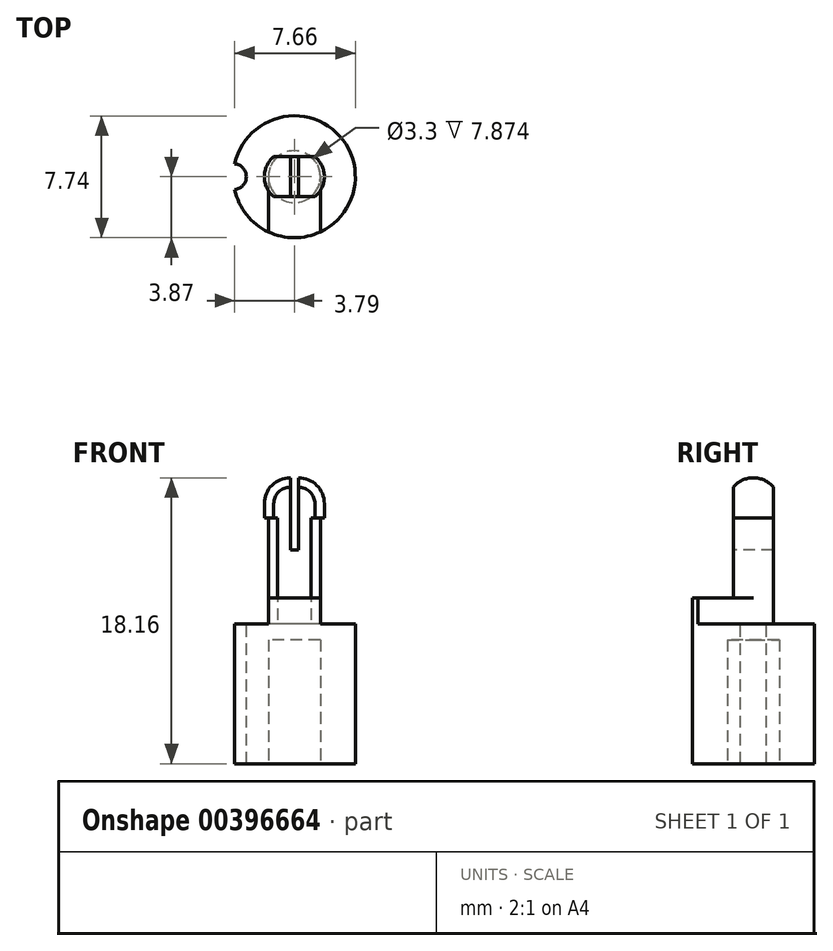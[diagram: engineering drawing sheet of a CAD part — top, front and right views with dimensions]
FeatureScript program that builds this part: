
annotation { "Feature Type Name" : "Feature", "Feature Type Description" : "" }
export const myFeature = defineFeature(function(context is Context, id is Id, definition is map)
    precondition{}
    {
        {
            var Q0;
            Q0=qCreatedBy(makeId("Top.planeOp"),FACE);
            var sketch = newSketch(context, id + "F0", { "sketchPlane" : qUnion([Q0])});
            skCircle(sketch, "E0", {"center": v(0, 0) * mm, "radius": 1.65 * mm});
            skCircle(sketch, "E1", {"center": v(0, 0) * mm, "radius": 3.87 * mm});
            skSolve(sketch);
        }
        {
            var Q0;
            Q0=makeQuery(id+"F0.imprint","IMPRINT",FACE,{"disambiguationData":[TD([[makeQuery(id+"F0.imprint","IMPRINT",EDGE,{"derivedFrom":sQuery(id+"F0.wireOp",EDGE,"E0")}),-1.0]])]});
            var Q1;
            Q1=sQuery(id+"F0.wireOp",EDGE,"E1");
            var Q2;
            Q2=sQuery(id+"F0.wireOp",EDGE,"E0");
            extrude(context, id + "F1", {"entities" : qUnion([Q0]), "surfaceEntities" : qUnion([Q1, Q2]), "depth" : 7.87 * mm});
        }
        {
            var Q0;
            Q0=makeQuery(id+"F1.opExtrude","CAP_FACE",FACE,{"disambiguationData":[OSD([sQuery(id+"F0.wireOp",EDGE,"E0"),sQuery(id+"F0.wireOp",EDGE,"E1")])],"isStart":false});
            var sketch = newSketch(context, id + "F2", { "sketchPlane" : qUnion([Q0])});
            skCircle(sketch, "E2", {"center": v(0, 0) * mm, "radius": 3.87 * mm});
            skSolve(sketch);
        }
        {
            var Q0;
            Q0 = qSketchRegion(id + "F2", true);
            extrude(context, id + "F3", {"entities" : qUnion([Q0]), "operationType" : NewBodyOperationType.ADD, "depth" : 1.02 * mm});
        }
        {
            var Q0;
            Q0=makeQuery(id+"F3.opExtrude","CAP_FACE",FACE,{"disambiguationData":[OSD([sQuery(id+"F2.wireOp",EDGE,"E2")])],"isStart":false});
            var sketch = newSketch(context, id + "F4", { "sketchPlane" : qUnion([Q0])});
            skCircle(sketch, "E3", {"center": v(-3.87, 0) * mm, "radius": 0.83 * mm});
            skLineSegment(sketch, "E4", {"start": v(-1.05, 1.27) * mm, "end": v(0, 1.27) * mm});
            skArc(sketch, "E5", {"start": v(-1.05, 1.27) * mm, "mid": v(-1.5, 0.7) * mm, "end": v(-1.65, 0) * mm});
            skLineSegment(sketch, "E6.MirrorCS", {"start": v(1.05, 1.27) * mm, "end": v(0, 1.27) * mm});
            skArc(sketch, "E7.MirrorCS", {"start": v(1.05, 1.27) * mm, "mid": v(1.5, 0.7) * mm, "end": v(1.65, 0) * mm});
            skLineSegment(sketch, "E8", {"start": v(-1.65, 0) * mm, "end": v(-1.65, -3.5) * mm});
            skLineSegment(sketch, "E9", {"start": v(1.65, 0) * mm, "end": v(1.65, -3.5) * mm});
            skSolve(sketch);
        }
        {
            var Q0;
            {var subQ0=sQuery(id+"F4.wireOp",EDGE,"E3");var subQ1=makeQuery(id+"F3.opExtrude","CAP_EDGE",EDGE,{"disambiguationData":[OSD([sQuery(id+"F2.wireOp",EDGE,"E2")])],"isStart":false});var subQ2=makeQuery(id+"F4.imprint","INTERSECT",VERTEX,{"disambiguationData":[OD(0.0)],"derivedFrom":[subQ1,subQ0]});Q0=makeQuery(id+"F4.imprint","IMPRINT",FACE,{"disambiguationData":[TD([[makeQuery(id+"F4.imprint","IMPRINT",EDGE,{"disambiguationData":[TD([[subQ2,-1.0]])],"derivedFrom":subQ0}),1.0]])]});}
            var Q1;
            Q1=makeQuery(id+"F1.opExtrude","CAP_FACE",FACE,{"disambiguationData":[OSD([sQuery(id+"F0.wireOp",EDGE,"E0"),sQuery(id+"F0.wireOp",EDGE,"E1")])],"isStart":true});
            extrude(context, id + "F5", {"entities" : qUnion([Q0]), "operationType" : NewBodyOperationType.REMOVE, "endBound" : BoundingType.UP_TO_SURFACE, "oppositeDirection" : true, "endBoundEntityFace" : qUnion([Q1]), "depth" : 25.4 * mm});
        }
        {
            var Q0;
            Q0=makeQuery(id+"F4.imprint","IMPRINT",FACE,{"disambiguationData":[TD([[makeQuery(id+"F4.imprint","IMPRINT",EDGE,{"derivedFrom":sQuery(id+"F4.wireOp",EDGE,"E4")}),-1.0]])]});
            extrude(context, id + "F6", {"entities" : qUnion([Q0]), "operationType" : NewBodyOperationType.ADD, "depth" : 1.65 * mm});
        }
        {
            var Q0;
            Q0=makeQuery(id+"F6.opExtrude","CAP_FACE",FACE,{"disambiguationData":[OSD([sQuery(id+"F2.wireOp",EDGE,"E2"),sQuery(id+"F4.wireOp",EDGE,"E4"),sQuery(id+"F4.wireOp",EDGE,"E5"),sQuery(id+"F4.wireOp",EDGE,"E6.MirrorCS"),sQuery(id+"F4.wireOp",EDGE,"E7.MirrorCS"),sQuery(id+"F4.wireOp",EDGE,"E8"),sQuery(id+"F4.wireOp",EDGE,"E9")])],"isStart":false});
            var sketch = newSketch(context, id + "F7", { "sketchPlane" : qUnion([Q0])});
            skCircle(sketch, "E10", {"center": v(-8.64, -1.16) * mm, "radius": 0.83 * mm});
            skLineSegment(sketch, "E11", {"start": v(-1.05, 1.27) * mm, "end": v(0, 1.27) * mm});
            skArc(sketch, "E12", {"start": v(-1.05, 1.27) * mm, "mid": v(-1.5, 0.7) * mm, "end": v(-1.65, 0) * mm});
            skLineSegment(sketch, "E13.MirrorCS", {"start": v(1.05, 1.27) * mm, "end": v(0, 1.27) * mm});
            skArc(sketch, "E14.MirrorCS", {"start": v(1.05, 1.27) * mm, "mid": v(1.5, 0.7) * mm, "end": v(1.65, 0) * mm});
            skLineSegment(sketch, "E15.MirrorCS", {"start": v(-1.05, -1.27) * mm, "end": v(0, -1.27) * mm});
            skArc(sketch, "E16.MirrorCS", {"start": v(-1.05, -1.27) * mm, "mid": v(-1.5, -0.7) * mm, "end": v(-1.65, 0) * mm});
            skLineSegment(sketch, "E17.MirrorCS", {"start": v(1.05, -1.27) * mm, "end": v(0, -1.27) * mm});
            skArc(sketch, "E18.MirrorCS", {"start": v(1.05, -1.27) * mm, "mid": v(1.5, -0.7) * mm, "end": v(1.65, 0) * mm});
            skSolve(sketch);
        }
        {
            var Q0;
            Q0=makeQuery(id+"F7.imprint","IMPRINT",FACE,{"disambiguationData":[TD([[makeQuery(id+"F7.imprint","IMPRINT",EDGE,{"derivedFrom":sQuery(id+"F7.wireOp",EDGE,"E11")}),1.0]])]});
            extrude(context, id + "F8", {"entities" : qUnion([Q0]), "operationType" : NewBodyOperationType.ADD, "depth" : 5.08 * mm});
        }
        {
            var Q0;
            Q0=makeQuery(id+"F8.opExtrude","CAP_FACE",FACE,{"disambiguationData":[OSD([sQuery(id+"F7.wireOp",EDGE,"E11"),sQuery(id+"F7.wireOp",EDGE,"E12"),sQuery(id+"F7.wireOp",EDGE,"E13.MirrorCS"),sQuery(id+"F7.wireOp",EDGE,"E14.MirrorCS"),sQuery(id+"F7.wireOp",EDGE,"E15.MirrorCS"),sQuery(id+"F7.wireOp",EDGE,"E16.MirrorCS"),sQuery(id+"F7.wireOp",EDGE,"E17.MirrorCS"),sQuery(id+"F7.wireOp",EDGE,"E18.MirrorCS")])],"isStart":false});
            var sketch = newSketch(context, id + "F9", { "sketchPlane" : qUnion([Q0])});
            skCircle(sketch, "E19", {"center": v(-9.4, -2.75) * mm, "radius": 0.83 * mm});
            skLineSegment(sketch, "E20", {"start": v(-1.3, 1.27) * mm, "end": v(-0.25, 1.27) * mm});
            skArc(sketch, "E21", {"start": v(-1.3, 1.27) * mm, "mid": v(-1.75, 0.7) * mm, "end": v(-1.9, 0) * mm});
            skLineSegment(sketch, "E22.MirrorCS", {"start": v(-1.3, -1.27) * mm, "end": v(-0.25, -1.27) * mm});
            skArc(sketch, "E23.MirrorCS", {"start": v(-1.3, -1.27) * mm, "mid": v(-1.75, -0.7) * mm, "end": v(-1.9, 0) * mm});
            skLineSegment(sketch, "E24", {"start": v(-0.25, 1.27) * mm, "end": v(-0.25, -1.27) * mm});
            skSolve(sketch);
        }
        {
            var Q0;
            {var subQ2=sQuery(id+"F9.wireOp",EDGE,"E24");Q0=makeQuery(id+"F9.imprint","IMPRINT",FACE,{"disambiguationData":[TD([[makeQuery(id+"F9.imprint","IMPRINT",EDGE,{"derivedFrom":subQ2}),-1.0]])]});}
            var Q1;
            {var subQ3=sQuery(id+"F9.wireOp",EDGE,"E21");Q1=makeQuery(id+"F9.imprint","IMPRINT",FACE,{"disambiguationData":[TD([[makeQuery(id+"F9.imprint","IMPRINT",EDGE,{"derivedFrom":subQ3}),1.0]])]});}
            extrude(context, id + "F10", {"entities" : qUnion([Q0, Q1]), "depth" : 2.54 * mm});
        }
        {
            var Q0;
            Q0=makeQuery(id+"F10.opExtrude","SWEPT_BODY",BODY,{"disambiguationData":[OSD([sQuery(id+"F9.wireOp",EDGE,"E20"),sQuery(id+"F9.wireOp",EDGE,"E21"),sQuery(id+"F9.wireOp",EDGE,"E22.MirrorCS"),sQuery(id+"F9.wireOp",EDGE,"E23.MirrorCS"),sQuery(id+"F9.wireOp",EDGE,"E24")])]});
            var Q1;
            Q1=qCreatedBy(makeId("Right.planeOp"),FACE);
            mirror(context, id + "F11", {"operationType" : NewBodyOperationType.ADD, "entities" : qUnion([Q0]), "mirrorPlane" : qUnion([Q1])});
        }
        {
            var Q0;
            Q0=makeQuery(id+"F8.opExtrude","CAP_FACE",FACE,{"disambiguationData":[OSD([sQuery(id+"F7.wireOp",EDGE,"E11"),sQuery(id+"F7.wireOp",EDGE,"E12"),sQuery(id+"F7.wireOp",EDGE,"E13.MirrorCS"),sQuery(id+"F7.wireOp",EDGE,"E14.MirrorCS"),sQuery(id+"F7.wireOp",EDGE,"E15.MirrorCS"),sQuery(id+"F7.wireOp",EDGE,"E16.MirrorCS"),sQuery(id+"F7.wireOp",EDGE,"E17.MirrorCS"),sQuery(id+"F7.wireOp",EDGE,"E18.MirrorCS")])],"isStart":false});
            var sketch = newSketch(context, id + "F12", { "sketchPlane" : qUnion([Q0])});
            skLineSegment(sketch, "E25.bottom", {"start": v(0.25, 1.27) * mm, "end": v(-0.25, 1.27) * mm});
            skLineSegment(sketch, "E25.top", {"start": v(0.25, -1.27) * mm, "end": v(-0.25, -1.27) * mm});
            skLineSegment(sketch, "E25.left", {"start": v(0.25, 1.27) * mm, "end": v(0.25, -1.27) * mm});
            skLineSegment(sketch, "E25.right", {"start": v(-0.25, 1.27) * mm, "end": v(-0.25, -1.27) * mm});
            skPoint(sketch, "E25.middle", {"position": v(0, 0) * mm});
            skSolve(sketch);
        }
        {
            var Q0;
            Q0=makeQuery(id+"F12.imprint","IMPRINT",FACE,{"disambiguationData":[TD([[makeQuery(id+"F12.imprint","IMPRINT",EDGE,{"derivedFrom":sQuery(id+"F12.wireOp",EDGE,"E25.bottom")}),1.0]])]});
            extrude(context, id + "F13", {"entities" : qUnion([Q0]), "operationType" : NewBodyOperationType.REMOVE, "oppositeDirection" : true, "depth" : 2.03 * mm});
        }
        {
            var Q0;
            Q0=makeQuery(id+"F10.opExtrude","CAP_EDGE",EDGE,{"disambiguationData":[OSD([sQuery(id+"F9.wireOp",EDGE,"E21"),sQuery(id+"F9.wireOp",EDGE,"E23.MirrorCS")])],"isStart":false});
            var Q1;
            Q1=makeQuery(id+"F11.opPattern","COPY",EDGE,{"derivedFrom":makeQuery(id+"F10.opExtrude","CAP_EDGE",EDGE,{"disambiguationData":[OSD([sQuery(id+"F9.wireOp",EDGE,"E21"),sQuery(id+"F9.wireOp",EDGE,"E23.MirrorCS")])],"isStart":false}),"instanceName":"1"});
            fillet(context, id + "F14", {"entities" : qUnion([Q0, Q1]), "radius" : 1.65 * mm, "tangentPropagation" : true, "allowEdgeOverflow" : false});
        }
    });
